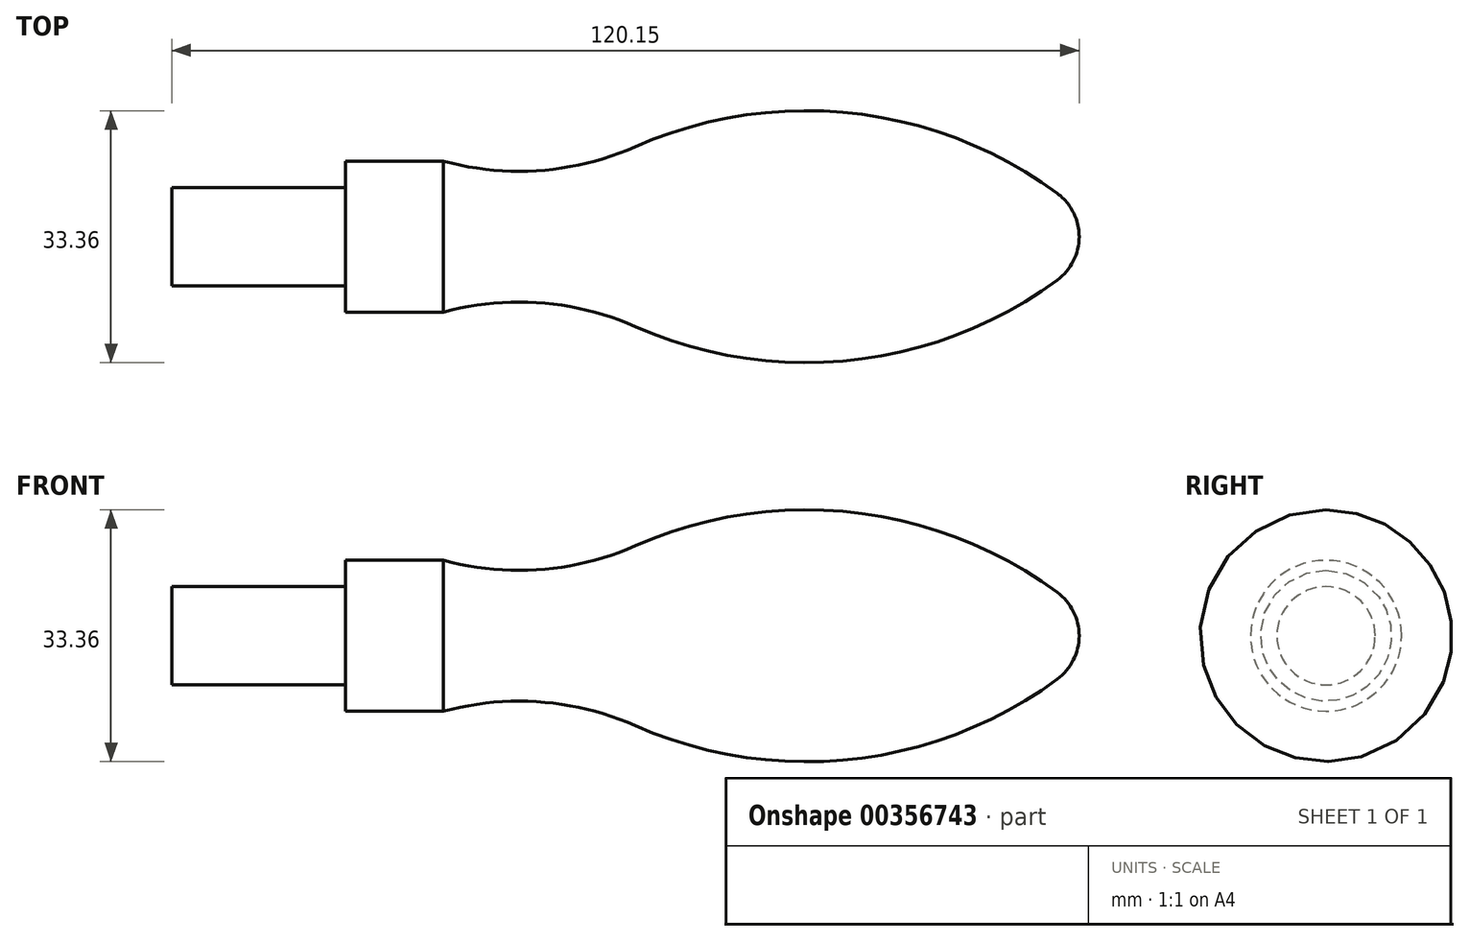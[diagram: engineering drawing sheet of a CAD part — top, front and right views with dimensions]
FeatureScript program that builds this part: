
annotation { "Feature Type Name" : "Feature", "Feature Type Description" : "" }
export const myFeature = defineFeature(function(context is Context, id is Id, definition is map)
    precondition{}
    {
        {
            var Q0;
            Q0=qCreatedBy(makeId("Top.planeOp"),FACE);
            var sketch = newSketch(context, id + "F0", { "sketchPlane" : qUnion([Q0])});
            skLineSegment(sketch, "E0.top", {"start": v(0, 6.5) * mm, "end": v(-23, 6.5) * mm});
            skLineSegment(sketch, "E0.left", {"start": v(0, 0) * mm, "end": v(0, 6.5) * mm});
            skLineSegment(sketch, "E0.right", {"start": v(-23, 0) * mm, "end": v(-23, 6.5) * mm});
            skLineSegment(sketch, "E1.MirrorCS", {"start": v(0, -6.5) * mm, "end": v(-23, -6.5) * mm});
            skLineSegment(sketch, "E2.MirrorCS", {"start": v(-23, 0) * mm, "end": v(-23, -6.5) * mm});
            skLineSegment(sketch, "E3.MirrorCS", {"start": v(0, 0) * mm, "end": v(0, -6.5) * mm});
            skLineSegment(sketch, "E4", {"start": v(61, 0) * mm, "end": v(61, 16.68) * mm, "construction": true});
            skLineSegment(sketch, "E5", {"start": v(0, 0) * mm, "end": v(0, 10) * mm});
            skLineSegment(sketch, "E6.MirrorCS", {"start": v(0, 0) * mm, "end": v(0, -10) * mm});
            skLineSegment(sketch, "E7", {"start": v(0, 10) * mm, "end": v(13, 10) * mm});
            skLineSegment(sketch, "E8.MirrorCS", {"start": v(0, -10) * mm, "end": v(13, -10) * mm});
            skArc(sketch, "E9", {"start": v(13, 10) * mm, "mid": v(25.84, 8.77) * mm, "end": v(38.36, 11.9) * mm});
            skPoint(sketch, "E10.endSnap0", {"position": v(42, 0) * mm});
            skArc(sketch, "E11", {"start": v(97.15, 0) * mm, "mid": v(96.38, 3.22) * mm, "end": v(94.24, 5.75) * mm});
            skArc(sketch, "E12.trimOffspring", {"start": v(94.24, 5.75) * mm, "mid": v(67.13, 16.35) * mm, "end": v(38.36, 11.9) * mm});
            skArc(sketch, "E13.MirrorCS", {"start": v(13, -10) * mm, "mid": v(25.84, -8.77) * mm, "end": v(38.36, -11.9) * mm});
            skArc(sketch, "E14.MirrorCS", {"start": v(94.24, -5.75) * mm, "mid": v(67.13, -16.35) * mm, "end": v(38.36, -11.9) * mm});
            skArc(sketch, "E15.MirrorCS", {"start": v(97.15, 0) * mm, "mid": v(96.38, -3.22) * mm, "end": v(94.24, -5.75) * mm});
            skPoint(sketch, "E16.orphan", {"position": v(23, 0) * mm});
            skLineSegment(sketch, "E17", {"start": v(-46.16, 0) * mm, "end": v(133.84, 0) * mm});
            skLineSegment(sketch, "E18", {"start": v(-23, 0) * mm, "end": v(0, 0) * mm});
            skSolve(sketch);
        }
        {
            var Q0;
            {var subQ0=sQuery(id+"F0.wireOp",EDGE,"E7");Q0=makeQuery(id+"F0.imprint","IMPRINT",FACE,{"disambiguationData":[TD([[makeQuery(id+"F0.imprint","IMPRINT",EDGE,{"derivedFrom":subQ0}),-1.0]])]});}
            var Q1;
            Q1=sQuery(id+"F0.wireOp",EDGE,"E17");
            revolve(context, id + "F1", {"entities" : qUnion([Q0]), "axis" : qUnion([Q1]), "revolveType" : RevolveType.FULL});
        }
        {
            var Q0;
            {var subQ0=sQuery(id+"F0.wireOp",EDGE,"E0.top");Q0=makeQuery(id+"F0.imprint","IMPRINT",FACE,{"disambiguationData":[TD([[makeQuery(id+"F0.imprint","IMPRINT",EDGE,{"derivedFrom":subQ0}),1.0]])]});}
            var Q1;
            Q1=sQuery(id+"F0.wireOp",EDGE,"E18");
            revolve(context, id + "F2", {"operationType" : NewBodyOperationType.ADD, "entities" : qUnion([Q0]), "axis" : qUnion([Q1]), "revolveType" : RevolveType.FULL});
        }
    });
